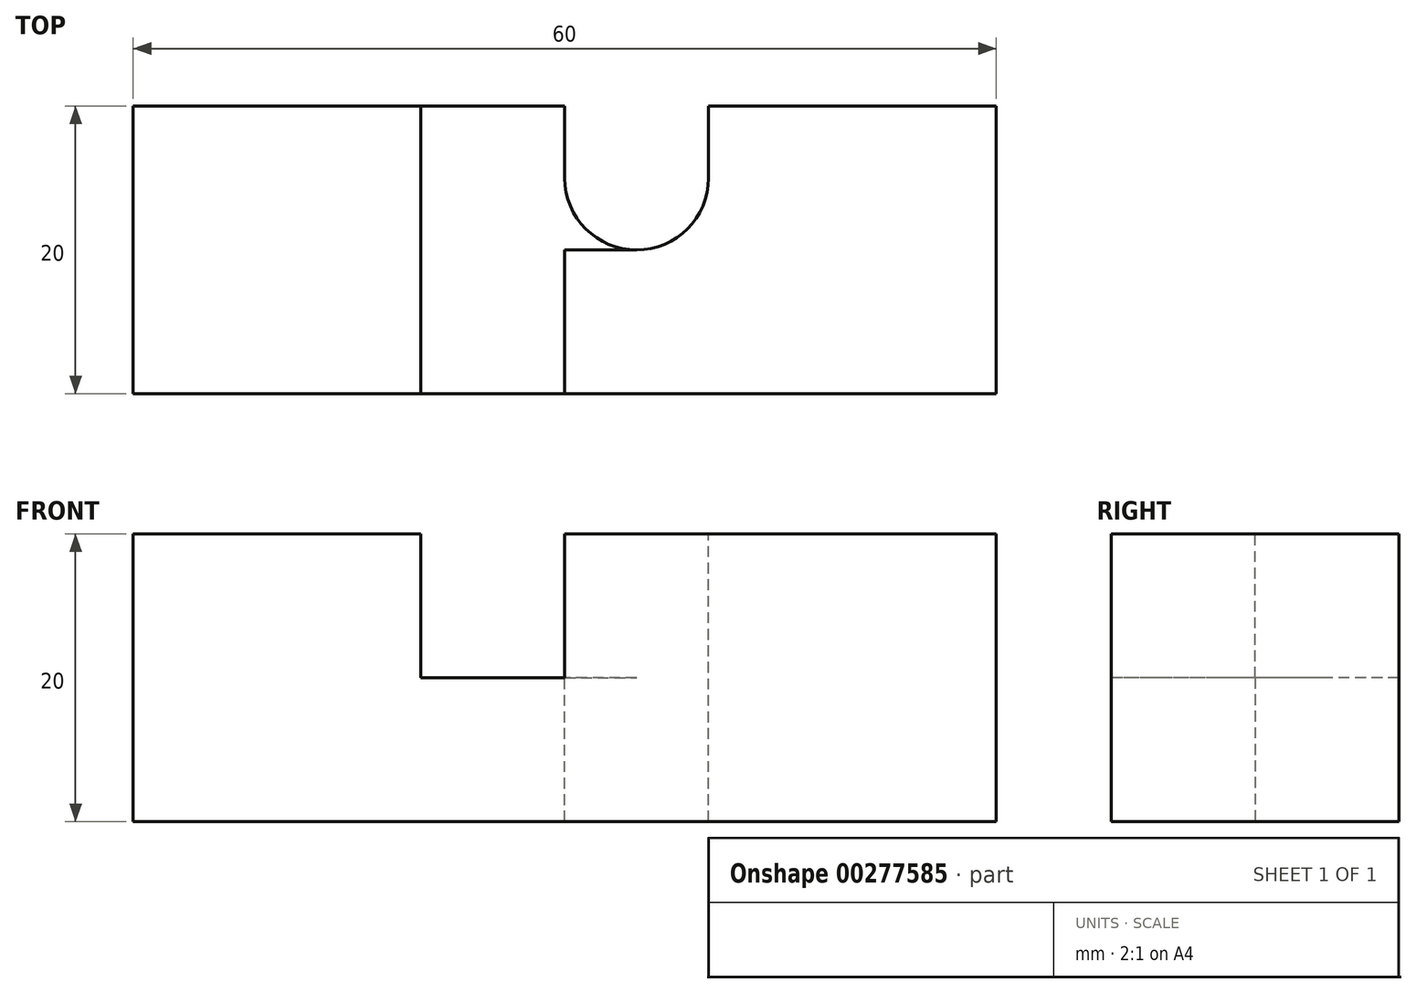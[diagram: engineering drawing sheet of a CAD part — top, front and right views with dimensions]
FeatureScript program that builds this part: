
annotation { "Feature Type Name" : "Feature", "Feature Type Description" : "" }
export const myFeature = defineFeature(function(context is Context, id is Id, definition is map)
    precondition{}
    {
        {
            var Q0;
            Q0=qCreatedBy(makeId("Top.planeOp"),FACE);
            var sketch = newSketch(context, id + "F0", { "sketchPlane" : qUnion([Q0])});
            skLineSegment(sketch, "E0.bottom", {"start": v(0, 0) * mm, "end": v(60, 0) * mm});
            skLineSegment(sketch, "E0.top", {"start": v(0, -20) * mm, "end": v(60, -20) * mm});
            skLineSegment(sketch, "E0.left", {"start": v(0, 0) * mm, "end": v(0, -20) * mm});
            skLineSegment(sketch, "E0.right", {"start": v(60, 0) * mm, "end": v(60, -20) * mm});
            skSolve(sketch);
        }
        {
            var Q0;
            Q0=makeQuery(id+"F0.imprint","IMPRINT",FACE,{"disambiguationData":[TD([[makeQuery(id+"F0.imprint","IMPRINT",EDGE,{"derivedFrom":sQuery(id+"F0.wireOp",EDGE,"E0.bottom")}),-1.0]])]});
            extrude(context, id + "F1", {"entities" : qUnion([Q0]), "depth" : 20 * mm});
        }
        {
            var Q0;
            Q0=makeQuery(id+"F1.opExtrude","CAP_FACE",FACE,{"disambiguationData":[OSD([sQuery(id+"F0.wireOp",EDGE,"E0.bottom"),sQuery(id+"F0.wireOp",EDGE,"E0.top"),sQuery(id+"F0.wireOp",EDGE,"E0.left"),sQuery(id+"F0.wireOp",EDGE,"E0.right")])],"isStart":false});
            var sketch = newSketch(context, id + "F2", { "sketchPlane" : qUnion([Q0])});
            skLineSegment(sketch, "E1.bottom", {"start": v(20, 0) * mm, "end": v(30, 0) * mm});
            skLineSegment(sketch, "E1.top", {"start": v(20, -20) * mm, "end": v(30, -20) * mm});
            skLineSegment(sketch, "E1.left", {"start": v(20, 0) * mm, "end": v(20, -20) * mm});
            skLineSegment(sketch, "E1.right", {"start": v(30, 0) * mm, "end": v(30, -20) * mm});
            skSolve(sketch);
        }
        {
            var Q0;
            Q0 = qSketchRegion(id + "F2", true);
            extrude(context, id + "F3", {"entities" : qUnion([Q0]), "operationType" : NewBodyOperationType.REMOVE, "oppositeDirection" : true, "depth" : 10 * mm});
        }
        {
            var Q0;
            {var subQ0=sQuery(id+"F0.wireOp",EDGE,"E0.bottom");var subQ1=sQuery(id+"F0.wireOp",EDGE,"E0.top");var subQ2=sQuery(id+"F0.wireOp",EDGE,"E0.right");Q0=makeQuery(id+"F3.boolean.opBoolean","SPLIT",FACE,{"disambiguationData":[TD([makeQuery(id+"F1.opExtrude","SWEPT_FACE",FACE,{"disambiguationData":[OSD([subQ2])]})])],"derivedFrom":makeQuery(id+"F1.opExtrude","CAP_FACE",FACE,{"disambiguationData":[OSD([subQ0,subQ1,sQuery(id+"F0.wireOp",EDGE,"E0.left"),subQ2])],"isStart":false})});}
            var sketch = newSketch(context, id + "F4", { "sketchPlane" : qUnion([Q0])});
            skPoint(sketch, "E2.oppositeSnap0", {"position": v(30, -10) * mm});
            skLineSegment(sketch, "E2.bottom", {"start": v(30, 0) * mm, "end": v(40, 0) * mm});
            skLineSegment(sketch, "E2.top", {"start": v(30, -10) * mm, "end": v(40, -10) * mm});
            skLineSegment(sketch, "E2.left", {"start": v(30, 0) * mm, "end": v(30, -10) * mm});
            skLineSegment(sketch, "E2.right", {"start": v(40, 0) * mm, "end": v(40, -10) * mm});
            skSolve(sketch);
        }
        {
            var Q0;
            Q0 = qSketchRegion(id + "F4", true);
            extrude(context, id + "F5", {"entities" : qUnion([Q0]), "operationType" : NewBodyOperationType.REMOVE, "oppositeDirection" : true, "depth" : 20 * mm});
        }
        {
            var Q0;
            {var subQ0=sQuery(id+"F4.wireOp",EDGE,"E2.top");var subQ1=sQuery(id+"F2.wireOp",EDGE,"E1.right");var subQ2=sQuery(id+"F4.wireOp",EDGE,"E2.left");Q0=makeQuery(id+"F5.boolean.opBoolean","COPY",EDGE,{"disambiguationData":[TD([makeQuery(id+"F1.opExtrude","CAP_FACE",FACE,{"disambiguationData":[OSD([sQuery(id+"F0.wireOp",EDGE,"E0.bottom"),sQuery(id+"F0.wireOp",EDGE,"E0.top"),sQuery(id+"F0.wireOp",EDGE,"E0.left"),sQuery(id+"F0.wireOp",EDGE,"E0.right")])],"isStart":true})])],"derivedFrom":makeQuery(id+"F5.opExtrude","SWEPT_EDGE",EDGE,{"disambiguationData":[OSD([subQ1,subQ0,subQ2])]})});}
            var Q1;
            Q1=makeQuery(id+"F5.boolean.opBoolean","COPY",EDGE,{"derivedFrom":makeQuery(id+"F5.opExtrude","SWEPT_EDGE",EDGE,{"disambiguationData":[OSD([sQuery(id+"F4.wireOp",EDGE,"E2.top"),sQuery(id+"F4.wireOp",EDGE,"E2.right")])]})});
            fillet(context, id + "F6", {"entities" : qUnion([Q0, Q1]), "radius" : 5 * mm, "tangentPropagation" : true, "allowEdgeOverflow" : false});
        }
    });
